# Revit family: ELR_ECLIO3_SQUARE_TRIM-FIX
name_source: partatom
category: Lighting Fixtures
units: mm (PartAtom-declared; Revit-internal decimal feet)

## family parameters
Always vertical = Yes
Cut with Voids When Loaded = No
Light Source = Yes
OmniClass Number = 23.80.70.00
OmniClass Title = Lighting
Part Type = Normal
Room Calculation Point = No
Round Connector Dimension = Use Diameter
Shared = No
Work Plane-Based = No

## types (4) — shared parameters
Color Filter = 16777215
Dimming Lamp Color Temperature Shift = <None>
Tilt Angle = 90.00°

## per-type parameters (varying)
| type | Photometric Web File |
| SQUARE ELR50P 10D 3000K ProART CRI95 | ECLIO-3 SQUARE ELR50P 10D 3000K ProART CRI95.ies |
| SQUARE ELR50P 20D 3000K ProART CRI95 | ECLIO-3 SQUARE ELR50P 20D 3000K ProART CRI95.ies |
| SQUARE ELR50P 35D 3000K ProART CRI95 | ECLIO-3 SQUARE ELR50P 35D 3000K ProART CRI95.ies |
| SQUARE ELR50P 60D 3000K ProART CRI95 | ECLIO-3 SQUARE ELR50P 60D 3000K ProART CRI95.ies |

## geometry (parser evidence)
native form markers: Sweep x2
no freeform markers — native parametric forms only
